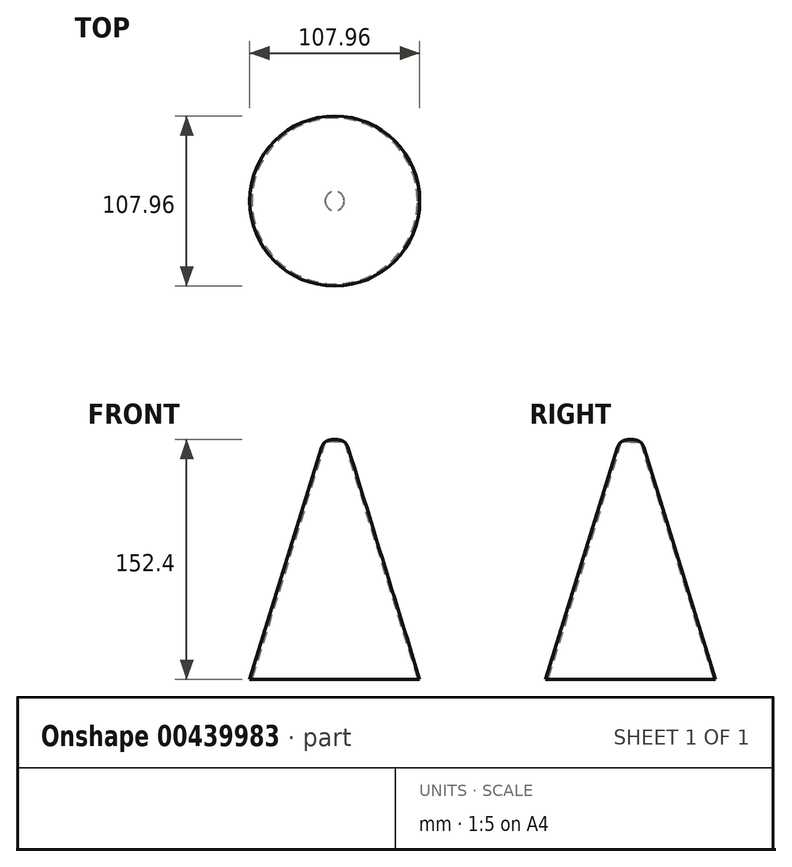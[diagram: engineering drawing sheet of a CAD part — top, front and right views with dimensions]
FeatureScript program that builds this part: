
annotation { "Feature Type Name" : "Feature", "Feature Type Description" : "" }
export const myFeature = defineFeature(function(context is Context, id is Id, definition is map)
    precondition{}
    {
        {
            var Q0;
            Q0=qCreatedBy(makeId("Front.planeOp"),FACE);
            var sketch = newSketch(context, id + "F0", { "sketchPlane" : qUnion([Q0])});
            skLineSegment(sketch, "E0", {"start": v(0, -49.92) * mm, "end": v(53.98, -49.92) * mm});
            skLineSegment(sketch, "E1", {"start": v(0, 102.48) * mm, "end": v(0, -49.92) * mm});
            skLineSegment(sketch, "E2", {"start": v(53.98, -49.92) * mm, "end": v(7.01, 102.1) * mm});
            skLineSegment(sketch, "E3", {"start": v(7.01, 102.1) * mm, "end": v(0, 102.48) * mm});
            skSolve(sketch);
        }
        {
            var Q0;
            Q0 = qSketchRegion(id + "F0", true);
            var Q1;
            Q1=sQuery(id+"F0.wireOp",EDGE,"E1");
            revolve(context, id + "F1", {"entities" : qUnion([Q0]), "axis" : qUnion([Q1]), "revolveType" : RevolveType.FULL});
        }
        {
            var Q0;
            Q0=makeQuery(id+"F1.opRevolve","SWEPT_FACE",FACE,{"disambiguationData":[OSD([sQuery(id+"F0.wireOp",EDGE,"E0")])]});
            shell(context, id + "F2", {"entities" : qUnion([Q0]), "thickness" : 1.27 * mm});
        }
        {
            var Q0;
            Q0=makeQuery(id+"F1.opRevolve","SWEPT_EDGE",EDGE,{"disambiguationData":[OSD([sQuery(id+"F0.wireOp",EDGE,"E2"),sQuery(id+"F0.wireOp",EDGE,"E3")])]});
            fillet(context, id + "F3", {"entities" : qUnion([Q0]), "radius" : 7.04 * mm, "tangentPropagation" : true, "allowEdgeOverflow" : false});
        }
    });
